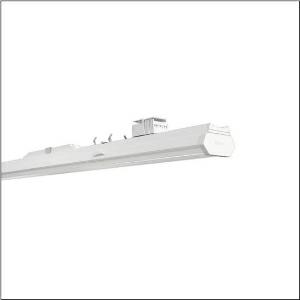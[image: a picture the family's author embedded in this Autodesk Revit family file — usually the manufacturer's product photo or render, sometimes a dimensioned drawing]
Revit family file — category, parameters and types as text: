
# Revit family: licross_r__21_protected_ho_52td12mn4e5m_88f3
name_source: partatom
category: Lighting Fixtures
units: mm (PartAtom-declared; Revit-internal decimal feet)

## family parameters
Cut with Voids When Loaded = No
Host = Face
Light Source = No
Part Type = Normal
Room Calculation Point = No
Round Connector Dimension = Use Diameter
Shared = No

## types (1)
- --- (1 x LED, 14780 lm, 83.2 W, 4000K)
    Apparent Load = 83 VA
    CIE Flux Codes = 70 91 97 98 100
    Color Rendering = 80
    Color Temperature = 4000K
    Default Elevation = 1800 mm
    Description = Licross® 21 Protected HO, luminaire insert, of sheet steel, galvanised, coil coated, white, length: 1.500mm, width: 90mm, height: 101mm, LED rated luminous flux: 14.790lm, light colour: 840, control gear: ON/OFF Multilumen, with plug, 3-pole, with phase selection, mains connection: 220..240V, AC, 50/60Hz, rated input power: 83W, internal wiring halogen-free, primary light control with lens, of plastic, primary optical cover: cover, of PMMA, light emission: direct distribution, primary light characteristic: symmetric, protection rating (complete): IP54, insulation class (complete): insulation class I (protective earthing), certification: CE, ENEC, VDE, UKCA, protection symbol: D if used in an environment with non-conductive dust loads with corresponding accessories, impact resistance: IK06, permissible ambient temperature for indoor applications: -35..+35°C, corresponds to IFS (International Featured Standards) requirements for safety and quality in the food industry, reducing of maximum allowable ambient temperature of 5°C with ceiling mounting, LABS conformity tested according to VDMA 24364:2018-05, packaging unit: 1 piece
    Height = 92 mm
    Lamp = 1 x LED
    Lamp Light Flux = 14780 lm
    Lamp Power = 83.2 W
    Lamp count = 1
    Length = 1500 mm
    Luminous efficacy = 178 lm/W
    Manufacturer = Siteco
    ModVariant = No
    Model = 52TD12MN4E5M
    Mounting Place = Ceiling
    Mounting Type = Pendant
    Number of Poles = 1
    OnlyDefault = Yes
    Power Factor = 1
    Product Name = Licross® 21 Protected HO
    Product group = luminaire insert | ceiling pendant
    ProductGroupID = 902
    Protection Class = Protection class I
    Protection Degree = IP 54
    RLX_Detail_Level = 1
    RLX_Emergency_Light_Flux = 0 lm
    RLX_Emergency_Type = 0
    RLX_Emergency_Type_DB = No
    RlxData = <blob elided: 22085 chars, md5=11813e0f>
    Socket = socket
    Standby Power = 0 W
    System Light Flux = 14780 lm
    System Power = 83 W
    Type Comments = factory setting: luminous flux: 100 % | (A | C | E) | 195 mA
    Type Image = l_1256148.jpg
    URL = http://relux.com
    VarID = @adj_130607
    Voltage = 0 V
    Weight = 0.00 kg
    Width = 88 mm

## geometry (parser evidence)
native form markers: Blend x4, Sweep x11
no freeform markers — native parametric forms only
